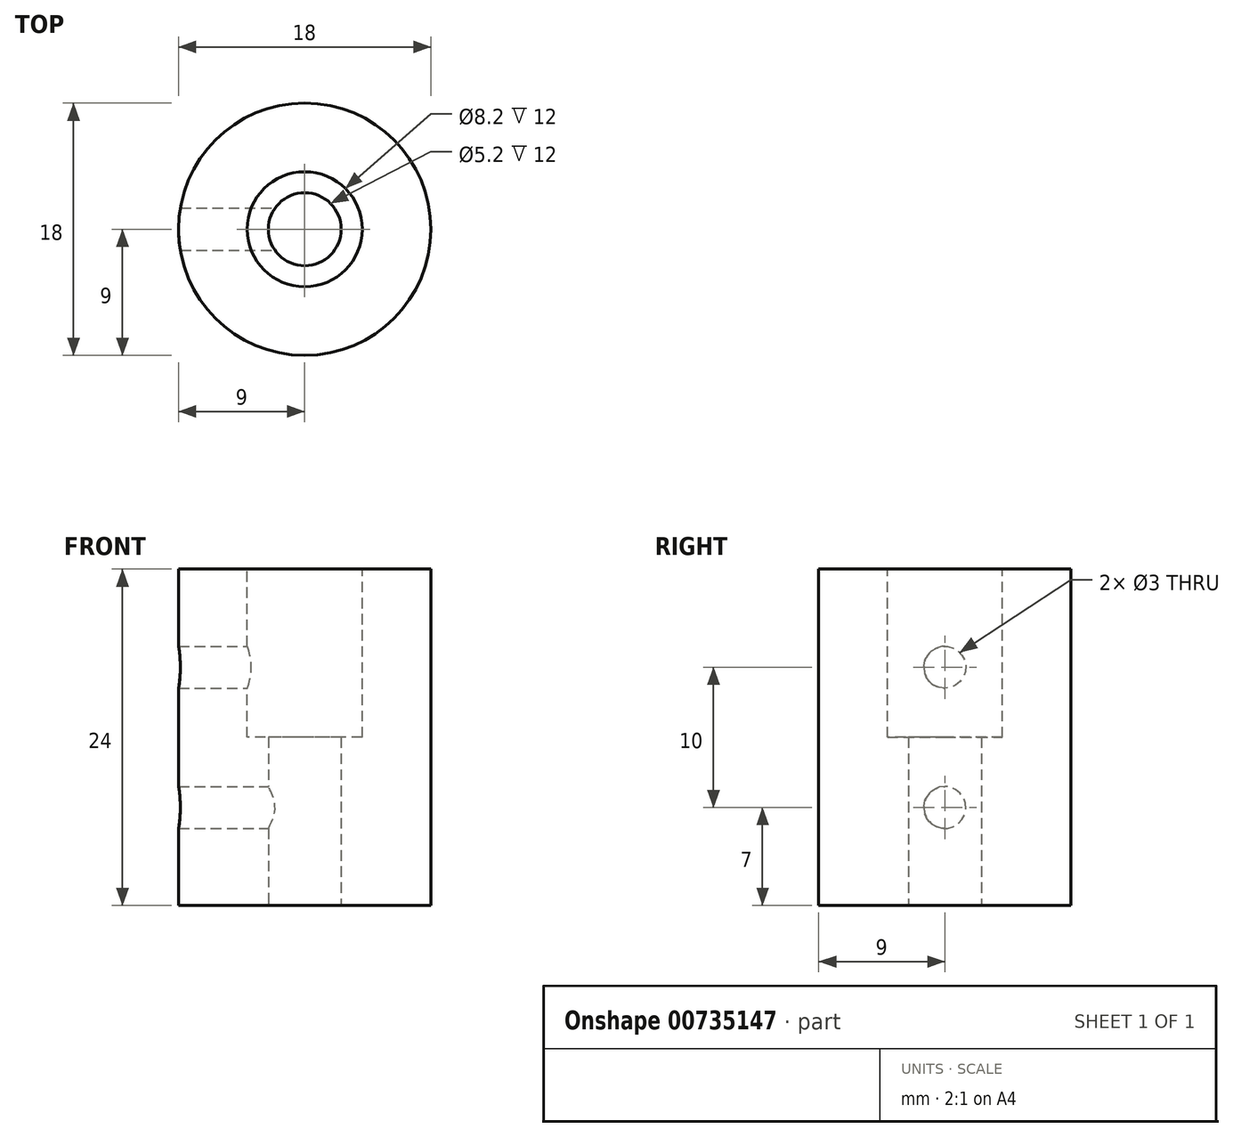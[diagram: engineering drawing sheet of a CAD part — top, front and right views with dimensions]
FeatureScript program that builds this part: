
annotation { "Feature Type Name" : "Feature", "Feature Type Description" : "" }
export const myFeature = defineFeature(function(context is Context, id is Id, definition is map)
    precondition{}
    {
        {
            var Q0;
            Q0=qCreatedBy(makeId("Top.planeOp"),FACE);
            var sketch = newSketch(context, id + "F0", { "sketchPlane" : qUnion([Q0])});
            skCircle(sketch, "E0", {"center": v(0, 0) * mm, "radius": 9 * mm});
            skSolve(sketch);
        }
        {
            var Q0;
            Q0=makeQuery(id+"F0.imprint","IMPRINT",FACE,{"disambiguationData":[TD([[makeQuery(id+"F0.imprint","IMPRINT",EDGE,{"derivedFrom":sQuery(id+"F0.wireOp",EDGE,"E0")}),1.0]])]});
            extrude(context, id + "F1", {"entities" : qUnion([Q0]), "depth" : 24 * mm, "offsetDistance" : 25 * mm});
        }
        {
            var Q0;
            Q0=makeQuery(id+"F1.opExtrude","CAP_FACE",FACE,{"disambiguationData":[OSD([sQuery(id+"F0.wireOp",EDGE,"E0")])],"isStart":false});
            var sketch = newSketch(context, id + "F2", { "sketchPlane" : qUnion([Q0])});
            skCircle(sketch, "E1", {"center": v(0, 0) * mm, "radius": 4.1 * mm});
            skSolve(sketch);
        }
        {
            var Q0;
            Q0=makeQuery(id+"F2.imprint","IMPRINT",FACE,{"disambiguationData":[TD([[makeQuery(id+"F2.imprint","IMPRINT",EDGE,{"derivedFrom":sQuery(id+"F2.wireOp",EDGE,"E1")}),1.0]])]});
            extrude(context, id + "F3", {"entities" : qUnion([Q0]), "operationType" : NewBodyOperationType.REMOVE, "oppositeDirection" : true, "depth" : 12 * mm, "offsetDistance" : 25 * mm});
        }
        {
            var Q0;
            Q0=makeQuery(id+"F1.opExtrude","CAP_FACE",FACE,{"disambiguationData":[OSD([sQuery(id+"F0.wireOp",EDGE,"E0")])],"isStart":true});
            var sketch = newSketch(context, id + "F4", { "sketchPlane" : qUnion([Q0])});
            skCircle(sketch, "E2", {"center": v(0, 0) * mm, "radius": 2.6 * mm});
            skSolve(sketch);
        }
        {
            var Q0;
            Q0=makeQuery(id+"F4.imprint","IMPRINT",FACE,{"disambiguationData":[TD([[makeQuery(id+"F4.imprint","IMPRINT",EDGE,{"derivedFrom":sQuery(id+"F4.wireOp",EDGE,"E2")}),1.0]])]});
            extrude(context, id + "F5", {"entities" : qUnion([Q0]), "operationType" : NewBodyOperationType.REMOVE, "oppositeDirection" : true, "depth" : 25 * mm, "offsetDistance" : 25 * mm});
        }
        {
            var Q0;
            Q0=qCreatedBy(makeId("Right.planeOp"),FACE);
            var sketch = newSketch(context, id + "F6", { "sketchPlane" : qUnion([Q0])});
            skCircle(sketch, "E3", {"center": v(0, 17) * mm, "radius": 1.5 * mm});
            skCircle(sketch, "E4", {"center": v(0, 7) * mm, "radius": 1.5 * mm});
            skSolve(sketch);
        }
        {
            var Q0;
            Q0=makeQuery(id+"F6.imprint","IMPRINT",FACE,{"disambiguationData":[TD([[makeQuery(id+"F6.imprint","IMPRINT",EDGE,{"derivedFrom":sQuery(id+"F6.wireOp",EDGE,"E3")}),1.0]])]});
            var Q1;
            Q1=makeQuery(id+"F6.imprint","IMPRINT",FACE,{"disambiguationData":[TD([[makeQuery(id+"F6.imprint","IMPRINT",EDGE,{"derivedFrom":sQuery(id+"F6.wireOp",EDGE,"E4")}),1.0]])]});
            extrude(context, id + "F7", {"entities" : qUnion([Q0, Q1]), "operationType" : NewBodyOperationType.REMOVE, "oppositeDirection" : true, "depth" : 25 * mm, "offsetDistance" : 25 * mm});
        }
    });
